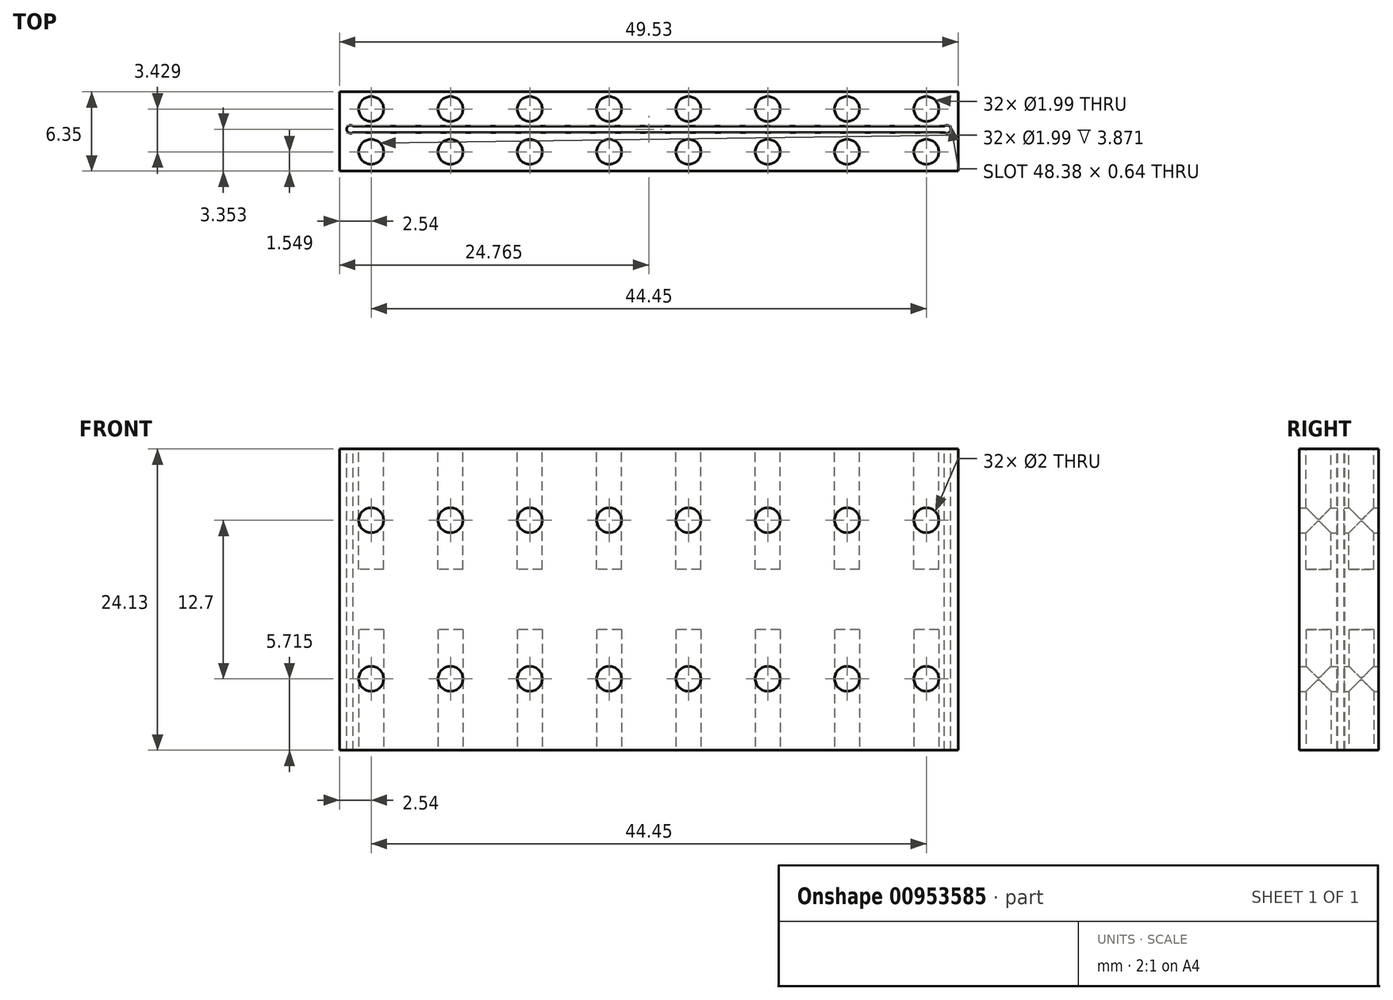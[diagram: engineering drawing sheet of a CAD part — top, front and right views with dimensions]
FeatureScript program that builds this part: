
annotation { "Feature Type Name" : "Feature", "Feature Type Description" : "" }
export const myFeature = defineFeature(function(context is Context, id is Id, definition is map)
    precondition{}
    {
        {
            var Q0;
            Q0=qCreatedBy(makeId("Front.planeOp"),FACE);
            var sketch = newSketch(context, id + "F0", { "sketchPlane" : qUnion([Q0])});
            skLineSegment(sketch, "E0.bottom", {"start": v(0, 0) * mm, "end": v(49.53, 0) * mm});
            skLineSegment(sketch, "E0.top", {"start": v(0, 24.13) * mm, "end": v(49.53, 24.13) * mm});
            skLineSegment(sketch, "E0.left", {"start": v(0, 0) * mm, "end": v(0, 24.13) * mm});
            skLineSegment(sketch, "E0.right", {"start": v(49.53, 0) * mm, "end": v(49.53, 24.13) * mm});
            skPoint(sketch, "E1", {"position": v(2.54, 5.71) * mm});
            skPoint(sketch, "E2", {"position": v(2.54, 18.41) * mm});
            skLineSegment(sketch, "E3", {"start": v(24.77, 24.13) * mm, "end": v(24.77, 0) * mm, "construction": true});
            skCircle(sketch, "E4", {"center": v(2.54, 18.41) * mm, "radius": 1 * mm});
            skCircle(sketch, "E5", {"center": v(2.54, 5.71) * mm, "radius": 1 * mm});
            skLineSegment(sketch, "E6", {"start": v(0, 12.07) * mm, "end": v(49.53, 12.07) * mm, "construction": true});
            skCircle(sketch, "E7.1.0.0", {"center": v(8.9, 18.41) * mm, "radius": 1 * mm});
            skCircle(sketch, "E7.1.0.1", {"center": v(8.9, 5.71) * mm, "radius": 1 * mm});
            skCircle(sketch, "E7.2.0.0", {"center": v(15.24, 18.41) * mm, "radius": 1 * mm});
            skCircle(sketch, "E7.2.0.1", {"center": v(15.24, 5.71) * mm, "radius": 1 * mm});
            skCircle(sketch, "E7.3.0.0", {"center": v(21.6, 18.41) * mm, "radius": 1 * mm});
            skCircle(sketch, "E7.3.0.1", {"center": v(21.6, 5.71) * mm, "radius": 1 * mm});
            skCircle(sketch, "E7.4.0.0", {"center": v(27.94, 18.41) * mm, "radius": 1 * mm});
            skCircle(sketch, "E7.4.0.1", {"center": v(27.94, 5.71) * mm, "radius": 1 * mm});
            skCircle(sketch, "E7.5.0.0", {"center": v(34.3, 18.41) * mm, "radius": 1 * mm});
            skCircle(sketch, "E7.5.0.1", {"center": v(34.3, 5.71) * mm, "radius": 1 * mm});
            skCircle(sketch, "E7.6.0.0", {"center": v(40.64, 18.41) * mm, "radius": 1 * mm});
            skCircle(sketch, "E7.6.0.1", {"center": v(40.64, 5.71) * mm, "radius": 1 * mm});
            skCircle(sketch, "E7.7.0.0", {"center": v(47, 18.41) * mm, "radius": 1 * mm});
            skCircle(sketch, "E7.7.0.1", {"center": v(47, 5.71) * mm, "radius": 1 * mm});
            skLineSegment(sketch, "E7.direction1", {"start": v(2.54, 18.41) * mm, "end": v(8.9, 18.41) * mm, "construction": true});
            skSolve(sketch);
        }
        {
            var Q0;
            Q0=makeQuery(id+"F0.imprint","IMPRINT",FACE,{"disambiguationData":[TD([[makeQuery(id+"F0.imprint","IMPRINT",EDGE,{"derivedFrom":sQuery(id+"F0.wireOp",EDGE,"E0.bottom")}),1.0]])]});
            extrude(context, id + "F1", {"entities" : qUnion([Q0]), "depth" : 6.35 * mm, "offsetDistance" : 25.4 * mm});
        }
        {
            var Q0;
            Q0=makeQuery(id+"F1.opExtrude","SWEPT_FACE",FACE,{"disambiguationData":[OSD([sQuery(id+"F0.wireOp",EDGE,"E0.top")])]});
            cPlane(context, id + "F2", {"entities" : qUnion([Q0]), "cplaneType" : CPlaneType.OFFSET, "offset" : 0.5 * mm, "width" : 152.4 * mm, "height" : 152.4 * mm});
        }
        {
            var Q0;
            Q0=qCreatedBy(id+"F2.planeOp",FACE);
            var sketch = newSketch(context, id + "F3", { "sketchPlane" : qUnion([Q0])});
            skLineSegment(sketch, "E8", {"start": v(-1.55, -3) * mm, "end": v(48.95, -3) * mm, "construction": true});
            skLineSegment(sketch, "E9.0", {"start": v(1.1, -3.25) * mm, "end": v(48.44, -3.25) * mm});
            skLineSegment(sketch, "E10.0", {"start": v(1.1, -2.74) * mm, "end": v(48.44, -2.74) * mm});
            skArc(sketch, "E11", {"start": v(48.44, -3.25) * mm, "mid": v(48.95, -3) * mm, "end": v(48.44, -2.74) * mm});
            skLineSegment(sketch, "E12", {"start": v(24.77, 2.6) * mm, "end": v(24.77, -10.48) * mm, "construction": true});
            skArc(sketch, "E13.MirrorCS", {"start": v(1.1, -3.25) * mm, "mid": v(0.58, -3) * mm, "end": v(1.1, -2.74) * mm});
            skSolve(sketch);
        }
        {
            var Q0;
            Q0=makeQuery(id+"F3.imprint","IMPRINT",FACE,{"disambiguationData":[TD([[makeQuery(id+"F3.imprint","IMPRINT",EDGE,{"derivedFrom":sQuery(id+"F3.wireOp",EDGE,"E9.0")}),1.0]])]});
            var Q1;
            Q1=makeQuery(id+"F1.opExtrude","SWEPT_FACE",FACE,{"disambiguationData":[OSD([sQuery(id+"F0.wireOp",EDGE,"E0.bottom")])]});
            extrude(context, id + "F4", {"entities" : qUnion([Q0]), "operationType" : NewBodyOperationType.REMOVE, "endBound" : BoundingType.UP_TO_SURFACE, "oppositeDirection" : true, "depth" : 25.4 * mm, "endBoundEntityFace" : qUnion([Q1]), "offsetDistance" : 25.4 * mm});
        }
        {
            var Q0;
            Q0=qCreatedBy(id+"F2.planeOp",FACE);
            var sketch = newSketch(context, id + "F5", { "sketchPlane" : qUnion([Q0])});
            skLineSegment(sketch, "E14", {"start": v(24.77, 2.24) * mm, "end": v(24.77, -8.67) * mm, "construction": true});
            skLineSegment(sketch, "E15", {"start": v(0, 0) * mm, "end": v(0, -2.74) * mm});
            skLineSegment(sketch, "E16", {"start": v(0, -6.35) * mm, "end": v(0, -3.25) * mm});
            skLineSegment(sketch, "E17", {"start": v(0, -1.37) * mm, "end": v(51.87, -1.37) * mm, "construction": true});
            skLineSegment(sketch, "E18", {"start": v(0, -4.8) * mm, "end": v(50.77, -4.8) * mm, "construction": true});
            skCircle(sketch, "E19", {"center": v(21.59, -1.37) * mm, "radius": 1 * mm});
            skCircle(sketch, "E20", {"center": v(21.59, -4.8) * mm, "radius": 1 * mm});
            skCircle(sketch, "E21.1.0.0", {"center": v(27.94, -1.37) * mm, "radius": 1 * mm});
            skCircle(sketch, "E21.1.0.1", {"center": v(27.94, -4.8) * mm, "radius": 1 * mm});
            skCircle(sketch, "E21.2.0.0", {"center": v(34.3, -1.37) * mm, "radius": 1 * mm});
            skCircle(sketch, "E21.2.0.1", {"center": v(34.3, -4.8) * mm, "radius": 1 * mm});
            skCircle(sketch, "E21.3.0.0", {"center": v(40.64, -1.37) * mm, "radius": 1 * mm});
            skCircle(sketch, "E21.3.0.1", {"center": v(40.64, -4.8) * mm, "radius": 1 * mm});
            skCircle(sketch, "E21.4.0.0", {"center": v(47, -1.37) * mm, "radius": 1 * mm});
            skCircle(sketch, "E21.4.0.1", {"center": v(47, -4.8) * mm, "radius": 1 * mm});
            skLineSegment(sketch, "E21.direction1", {"start": v(21.59, -1.37) * mm, "end": v(27.94, -1.37) * mm, "construction": true});
            skCircle(sketch, "E22.1.0.0", {"center": v(15.24, -1.37) * mm, "radius": 1 * mm});
            skCircle(sketch, "E22.1.0.1", {"center": v(15.24, -4.8) * mm, "radius": 1 * mm});
            skCircle(sketch, "E22.2.0.0", {"center": v(8.89, -1.37) * mm, "radius": 1 * mm});
            skCircle(sketch, "E22.2.0.1", {"center": v(8.89, -4.8) * mm, "radius": 1 * mm});
            skCircle(sketch, "E22.3.0.0", {"center": v(2.54, -1.37) * mm, "radius": 1 * mm});
            skCircle(sketch, "E22.3.0.1", {"center": v(2.54, -4.8) * mm, "radius": 1 * mm});
            skLineSegment(sketch, "E22.direction1", {"start": v(21.59, -1.37) * mm, "end": v(15.24, -1.37) * mm, "construction": true});
            skSolve(sketch);
        }
        {
            var Q0;
            Q0=makeQuery(id+"F5.imprint","IMPRINT",FACE,{"disambiguationData":[TD([[makeQuery(id+"F5.imprint","IMPRINT",EDGE,{"derivedFrom":sQuery(id+"F5.wireOp",EDGE,"E22.3.0.0")}),1.0]])]});
            var Q1;
            Q1=makeQuery(id+"F5.imprint","IMPRINT",FACE,{"disambiguationData":[TD([[makeQuery(id+"F5.imprint","IMPRINT",EDGE,{"derivedFrom":sQuery(id+"F5.wireOp",EDGE,"E22.2.0.0")}),1.0]])]});
            var Q2;
            Q2=makeQuery(id+"F5.imprint","IMPRINT",FACE,{"disambiguationData":[TD([[makeQuery(id+"F5.imprint","IMPRINT",EDGE,{"derivedFrom":sQuery(id+"F5.wireOp",EDGE,"E22.1.0.0")}),1.0]])]});
            var Q3;
            Q3=makeQuery(id+"F5.imprint","IMPRINT",FACE,{"disambiguationData":[TD([[makeQuery(id+"F5.imprint","IMPRINT",EDGE,{"derivedFrom":sQuery(id+"F5.wireOp",EDGE,"E19")}),1.0]])]});
            var Q4;
            Q4=makeQuery(id+"F5.imprint","IMPRINT",FACE,{"disambiguationData":[TD([[makeQuery(id+"F5.imprint","IMPRINT",EDGE,{"derivedFrom":sQuery(id+"F5.wireOp",EDGE,"E21.1.0.0")}),1.0]])]});
            var Q5;
            Q5=makeQuery(id+"F5.imprint","IMPRINT",FACE,{"disambiguationData":[TD([[makeQuery(id+"F5.imprint","IMPRINT",EDGE,{"derivedFrom":sQuery(id+"F5.wireOp",EDGE,"E21.2.0.0")}),1.0]])]});
            var Q6;
            Q6=makeQuery(id+"F5.imprint","IMPRINT",FACE,{"disambiguationData":[TD([[makeQuery(id+"F5.imprint","IMPRINT",EDGE,{"derivedFrom":sQuery(id+"F5.wireOp",EDGE,"E21.3.0.0")}),1.0]])]});
            var Q7;
            Q7=makeQuery(id+"F5.imprint","IMPRINT",FACE,{"disambiguationData":[TD([[makeQuery(id+"F5.imprint","IMPRINT",EDGE,{"derivedFrom":sQuery(id+"F5.wireOp",EDGE,"E21.4.0.0")}),1.0]])]});
            var Q8;
            Q8=makeQuery(id+"F5.imprint","IMPRINT",FACE,{"disambiguationData":[TD([[makeQuery(id+"F5.imprint","IMPRINT",EDGE,{"derivedFrom":sQuery(id+"F5.wireOp",EDGE,"E21.4.0.1")}),1.0]])]});
            var Q9;
            Q9=makeQuery(id+"F5.imprint","IMPRINT",FACE,{"disambiguationData":[TD([[makeQuery(id+"F5.imprint","IMPRINT",EDGE,{"derivedFrom":sQuery(id+"F5.wireOp",EDGE,"E21.3.0.1")}),1.0]])]});
            var Q10;
            Q10=makeQuery(id+"F5.imprint","IMPRINT",FACE,{"disambiguationData":[TD([[makeQuery(id+"F5.imprint","IMPRINT",EDGE,{"derivedFrom":sQuery(id+"F5.wireOp",EDGE,"E21.2.0.1")}),1.0]])]});
            var Q11;
            Q11=makeQuery(id+"F5.imprint","IMPRINT",FACE,{"disambiguationData":[TD([[makeQuery(id+"F5.imprint","IMPRINT",EDGE,{"derivedFrom":sQuery(id+"F5.wireOp",EDGE,"E21.1.0.1")}),1.0]])]});
            var Q12;
            Q12=makeQuery(id+"F5.imprint","IMPRINT",FACE,{"disambiguationData":[TD([[makeQuery(id+"F5.imprint","IMPRINT",EDGE,{"derivedFrom":sQuery(id+"F5.wireOp",EDGE,"E20")}),1.0]])]});
            var Q13;
            Q13=makeQuery(id+"F5.imprint","IMPRINT",FACE,{"disambiguationData":[TD([[makeQuery(id+"F5.imprint","IMPRINT",EDGE,{"derivedFrom":sQuery(id+"F5.wireOp",EDGE,"E22.1.0.1")}),1.0]])]});
            var Q14;
            Q14=makeQuery(id+"F5.imprint","IMPRINT",FACE,{"disambiguationData":[TD([[makeQuery(id+"F5.imprint","IMPRINT",EDGE,{"derivedFrom":sQuery(id+"F5.wireOp",EDGE,"E22.2.0.1")}),1.0]])]});
            var Q15;
            Q15=makeQuery(id+"F5.imprint","IMPRINT",FACE,{"disambiguationData":[TD([[makeQuery(id+"F5.imprint","IMPRINT",EDGE,{"derivedFrom":sQuery(id+"F5.wireOp",EDGE,"E22.3.0.1")}),1.0]])]});
            extrude(context, id + "F6", {"entities" : qUnion([Q0, Q1, Q2, Q3, Q4, Q5, Q6, Q7, Q8, Q9, Q10, Q11, Q12, Q13, Q14, Q15]), "operationType" : NewBodyOperationType.REMOVE, "oppositeDirection" : true, "depth" : 10.16 * mm, "offsetDistance" : 25.4 * mm});
        }
        {
            var Q0;
            Q0=makeQuery(id+"F1.opExtrude","SWEPT_FACE",FACE,{"disambiguationData":[OSD([sQuery(id+"F0.wireOp",EDGE,"E0.top")])]});
            var Q1;
            Q1=makeQuery(id+"F1.opExtrude","SWEPT_FACE",FACE,{"disambiguationData":[OSD([sQuery(id+"F0.wireOp",EDGE,"E0.bottom")])]});
            cPlane(context, id + "F7", {"entities" : qUnion([Q0, Q1]), "cplaneType" : CPlaneType.MID_PLANE, "offset" : 25.4 * mm, "width" : 152.4 * mm, "height" : 152.4 * mm});
        }
        {
            var Q0;
            Q0=qCreatedBy(makeId("Top.planeOp"),FACE);
            var sketch = newSketch(context, id + "F8", { "sketchPlane" : qUnion([Q0])});
            skLineSegment(sketch, "E23.bottom", {"start": v(-12.73, -19.04) * mm, "end": v(66.17, -19.04) * mm});
            skLineSegment(sketch, "E23.top", {"start": v(-12.73, 17.36) * mm, "end": v(66.17, 17.36) * mm});
            skLineSegment(sketch, "E23.left", {"start": v(-12.73, -19.04) * mm, "end": v(-12.73, 17.36) * mm});
            skLineSegment(sketch, "E23.right", {"start": v(66.17, -19.04) * mm, "end": v(66.17, 17.36) * mm});
            skSolve(sketch);
        }
        {
            var Q0;
            Q0=makeQuery(id+"F8.imprint","IMPRINT",FACE,{"disambiguationData":[TD([[makeQuery(id+"F8.imprint","IMPRINT",EDGE,{"derivedFrom":sQuery(id+"F8.wireOp",EDGE,"E23.bottom")}),1.0]])]});
            extrude(context, id + "F9", {"entities" : qUnion([Q0]), "operationType" : NewBodyOperationType.REMOVE, "depth" : 12.06 * mm, "offsetDistance" : 25.4 * mm});
        }
        {
            var Q0;
            Q0=makeQuery(id+"F1.opExtrude","SWEPT_BODY",BODY,{"disambiguationData":[OSD([sQuery(id+"F0.wireOp",EDGE,"E0.bottom"),sQuery(id+"F0.wireOp",EDGE,"E0.top"),sQuery(id+"F0.wireOp",EDGE,"E0.left"),sQuery(id+"F0.wireOp",EDGE,"E0.right"),sQuery(id+"F0.wireOp",EDGE,"E4"),sQuery(id+"F0.wireOp",EDGE,"E5"),sQuery(id+"F0.wireOp",EDGE,"E7.1.0.0"),sQuery(id+"F0.wireOp",EDGE,"E7.1.0.1"),sQuery(id+"F0.wireOp",EDGE,"E7.2.0.0"),sQuery(id+"F0.wireOp",EDGE,"E7.2.0.1"),sQuery(id+"F0.wireOp",EDGE,"E7.3.0.0"),sQuery(id+"F0.wireOp",EDGE,"E7.3.0.1"),sQuery(id+"F0.wireOp",EDGE,"E7.4.0.0"),sQuery(id+"F0.wireOp",EDGE,"E7.4.0.1"),sQuery(id+"F0.wireOp",EDGE,"E7.5.0.0"),sQuery(id+"F0.wireOp",EDGE,"E7.5.0.1"),sQuery(id+"F0.wireOp",EDGE,"E7.6.0.0"),sQuery(id+"F0.wireOp",EDGE,"E7.6.0.1"),sQuery(id+"F0.wireOp",EDGE,"E7.7.0.0"),sQuery(id+"F0.wireOp",EDGE,"E7.7.0.1")])]});
            var Q1;
            Q1=qCreatedBy(id+"F7.planeOp",FACE);
            mirror(context, id + "F10", {"operationType" : NewBodyOperationType.ADD, "entities" : qUnion([Q0]), "mirrorPlane" : qUnion([Q1])});
        }
    });
